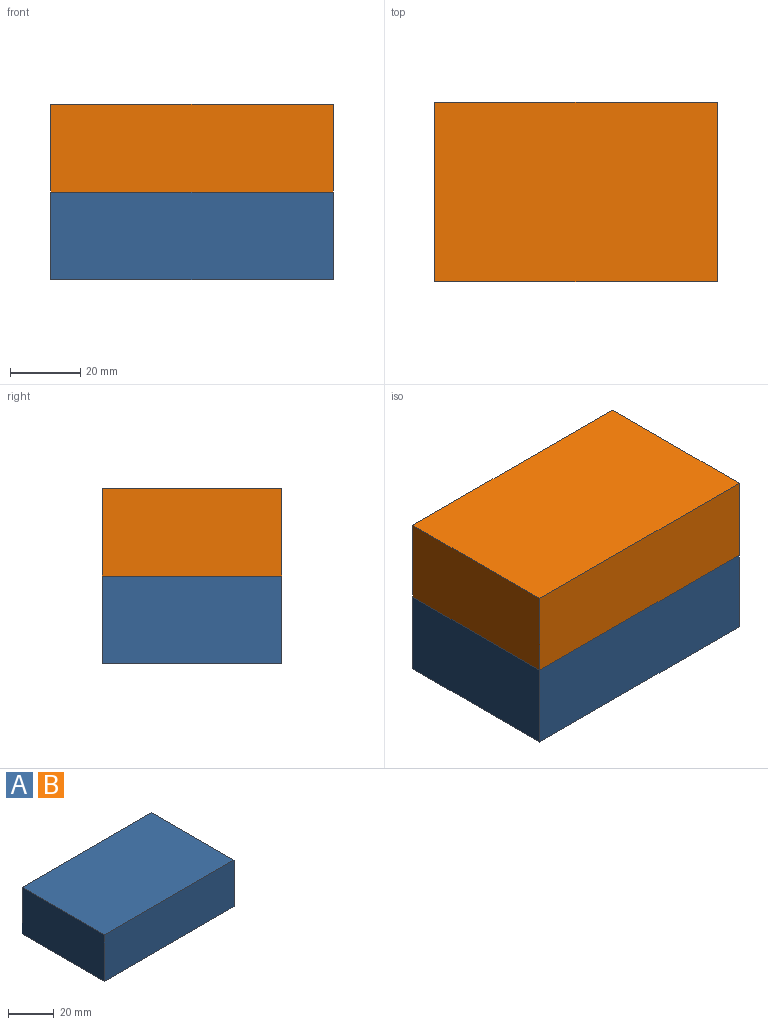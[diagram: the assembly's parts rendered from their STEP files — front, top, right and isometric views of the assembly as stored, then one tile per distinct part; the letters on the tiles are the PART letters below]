
ASSEMBLY  parts=2 mates=1
PART A: 6 faces, bbox 80.3x51.1x25 mm
  f0: plane 80.35x25mm, normal (0,1,0), area 2008.6mm2, adj f1,f3,f4,f5
  f1: plane 51.05x25mm, normal (-1,0,0), area 1276.3mm2, adj f0,f2,f4,f5
  f2: plane 80.35x25mm, normal (0,-1,0), area 2008.6mm2, adj f1,f3,f4,f5
  f3: plane 51.05x25mm, normal (1,0,0), area 1276.3mm2, adj f0,f2,f4,f5
  f4: plane 80.35x51.05mm, normal (0,0,1), area 4101.8mm2, adj f0,f1,f2,f3
  f5: plane 80.35x51.05mm, normal (0,0,-1), area 4101.8mm2, adj f0,f1,f2,f3
PART B: same geometry as A
PLACE A t=(-4.08,36.36,32.61)mm
PLACE B t=(-4.08,36.36,57.61)mm
MATE planar A.f4 <-> B.f5  axis (0,0,1) through (36.1,10.83,57.61)mm
